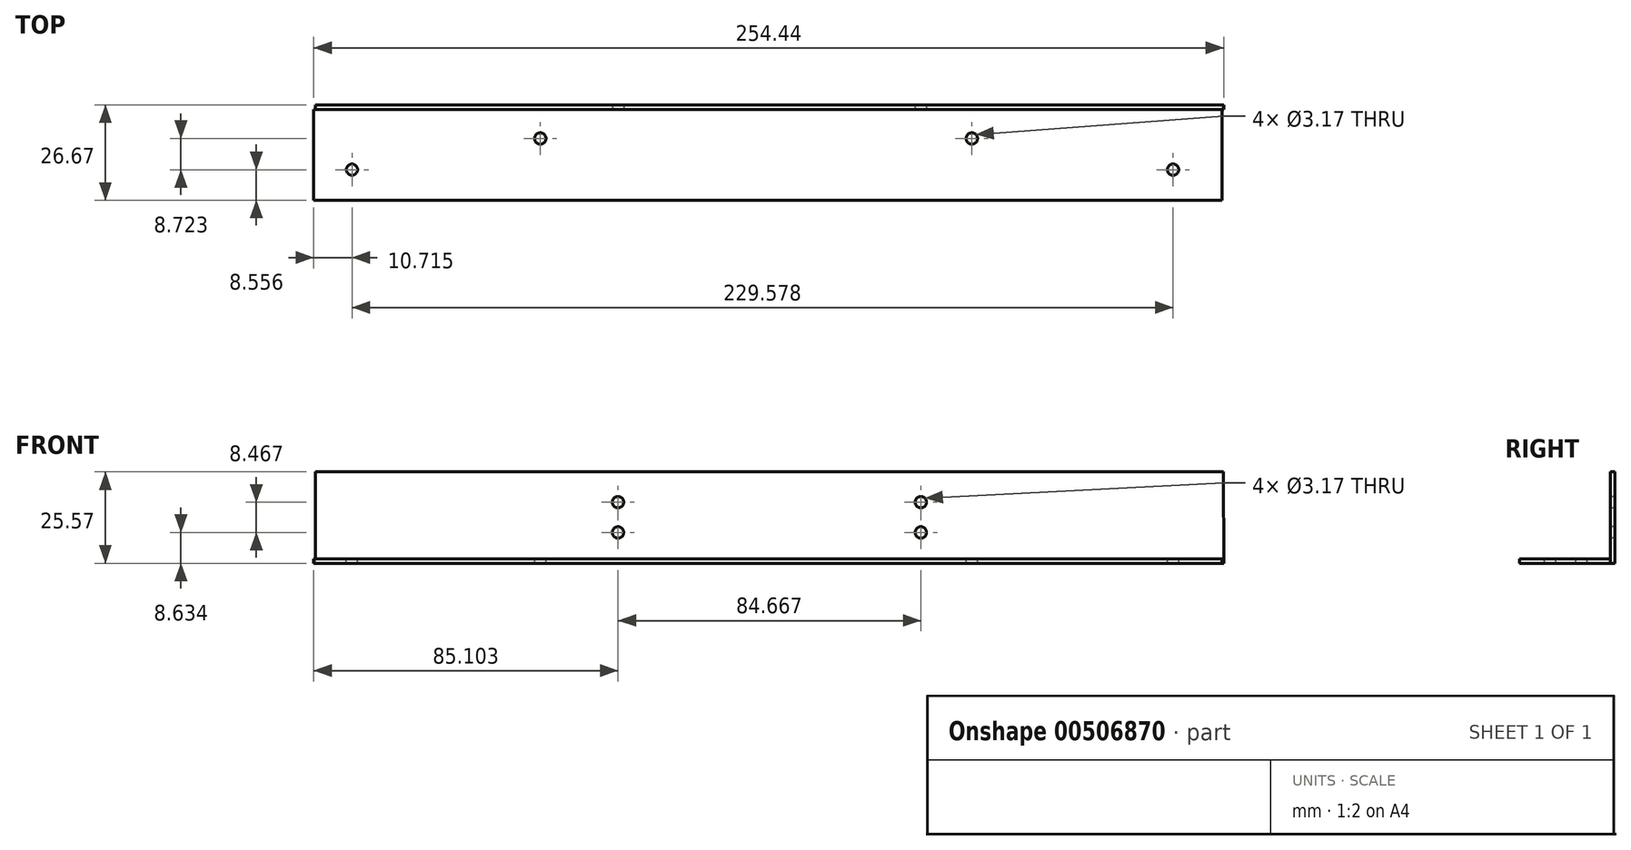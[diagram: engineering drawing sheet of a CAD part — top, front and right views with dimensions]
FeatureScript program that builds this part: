
annotation { "Feature Type Name" : "Feature", "Feature Type Description" : "" }
export const myFeature = defineFeature(function(context is Context, id is Id, definition is map)
    precondition{}
    {
        {
            var Q0;
            Q0=qCreatedBy(makeId("Front.planeOp"),FACE);
            var sketch = newSketch(context, id + "F0", { "sketchPlane" : qUnion([Q0])});
            skLineSegment(sketch, "E0", {"start": v(-131.8, 0) * mm, "end": v(122.2, 0) * mm});
            skLineSegment(sketch, "E1", {"start": v(-131.8, 0) * mm, "end": v(-131.8, 25.57) * mm});
            skLineSegment(sketch, "E2", {"start": v(-131.8, 25.57) * mm, "end": v(122.12, 25.57) * mm});
            skLineSegment(sketch, "E3", {"start": v(122.12, 25.57) * mm, "end": v(122.2, 0) * mm});
            skLineSegment(sketch, "E4", {"start": v(-47.14, 25.57) * mm, "end": v(-47.14, 0) * mm});
            skLineSegment(sketch, "E5", {"start": v(37.53, 25.57) * mm, "end": v(37.53, 0) * mm});
            skLineSegment(sketch, "E6", {"start": v(-47.14, 17.1) * mm, "end": v(37.53, 17.1) * mm});
            skLineSegment(sketch, "E7", {"start": v(-47.14, 8.63) * mm, "end": v(37.53, 8.63) * mm});
            skSolve(sketch);
        }
        {
            var Q0;
            Q0=qCreatedBy(makeId("Top.planeOp"),FACE);
            var sketch = newSketch(context, id + "F1", { "sketchPlane" : qUnion([Q0])});
            skLineSegment(sketch, "E8.bottom", {"start": v(-132.24, 0) * mm, "end": v(121.76, 0) * mm});
            skLineSegment(sketch, "E8.top", {"start": v(-132.24, -25.4) * mm, "end": v(121.76, -25.4) * mm});
            skLineSegment(sketch, "E8.left", {"start": v(-132.24, 0) * mm, "end": v(-132.24, -25.4) * mm});
            skLineSegment(sketch, "E8.right", {"start": v(121.76, 0) * mm, "end": v(121.76, -25.4) * mm});
            skLineSegment(sketch, "E9", {"start": v(-68.74, 0) * mm, "end": v(-68.74, -25.4) * mm, "construction": true});
            skLineSegment(sketch, "E10", {"start": v(-5.24, 0) * mm, "end": v(-5.24, -25.4) * mm, "construction": true});
            skLineSegment(sketch, "E11", {"start": v(58.26, 0) * mm, "end": v(58.26, -25.4) * mm, "construction": true});
            skLineSegment(sketch, "E12", {"start": v(-132.24, -8.47) * mm, "end": v(121.76, -8.47) * mm, "construction": true});
            skLineSegment(sketch, "E13", {"start": v(-132.24, -16.93) * mm, "end": v(121.76, -16.93) * mm, "construction": true});
            skSolve(sketch);
        }
        {
            var Q0;
            Q0=makeQuery(id+"F0.imprint","IMPRINT",FACE,{"disambiguationData":[TD([[makeQuery(id+"F0.imprint","IMPRINT",EDGE,{"derivedFrom":sQuery(id+"F0.wireOp",EDGE,"E0")}),1.0]])]});
            var Q1;
            {var subQ1=sQuery(id+"F0.wireOp",EDGE,"E1");Q1=makeQuery(id+"F0.imprint","IMPRINT",FACE,{"disambiguationData":[TD([[makeQuery(id+"F0.imprint","IMPRINT",EDGE,{"derivedFrom":subQ1}),-1.0]])]});}
            var Q2;
            {var subQ5=sQuery(id+"F0.wireOp",EDGE,"E6");Q2=makeQuery(id+"F0.imprint","IMPRINT",FACE,{"disambiguationData":[TD([[makeQuery(id+"F0.imprint","IMPRINT",EDGE,{"derivedFrom":subQ5}),1.0]])]});}
            var Q3;
            {var subQ0=sQuery(id+"F0.wireOp",EDGE,"E6");Q3=makeQuery(id+"F0.imprint","IMPRINT",FACE,{"disambiguationData":[TD([[makeQuery(id+"F0.imprint","IMPRINT",EDGE,{"derivedFrom":subQ0}),-1.0]])]});}
            var Q4;
            {var subQ4=sQuery(id+"F0.wireOp",EDGE,"E3");Q4=makeQuery(id+"F0.imprint","IMPRINT",FACE,{"disambiguationData":[TD([[makeQuery(id+"F0.imprint","IMPRINT",EDGE,{"derivedFrom":subQ4}),-1.0]])]});}
            extrude(context, id + "F2", {"entities" : qUnion([Q0, Q1, Q2, Q3, Q4]), "oppositeDirection" : true, "depth" : 1.27 * mm, "offsetDistance" : 25.4 * mm});
        }
        {
            var Q0;
            Q0=makeQuery(id+"F1.imprint","IMPRINT",FACE,{"disambiguationData":[TD([[makeQuery(id+"F1.imprint","IMPRINT",EDGE,{"derivedFrom":sQuery(id+"F1.wireOp",EDGE,"E8.bottom")}),-1.0]])]});
            extrude(context, id + "F3", {"entities" : qUnion([Q0]), "operationType" : NewBodyOperationType.ADD, "depth" : 1.27 * mm, "offsetDistance" : 25.4 * mm});
        }
        {
            var Q0;
            Q0=sQuery(id+"F0.wireOp",VERTEX,"E7.start");
            var Q1;
            Q1=sQuery(id+"F0.wireOp",VERTEX,"E7.end");
            var Q2;
            Q2=sQuery(id+"F0.wireOp",VERTEX,"E6.end");
            var Q3;
            Q3=sQuery(id+"F0.wireOp",VERTEX,"E6.start");
            var Q4;
            Q4=makeQuery(id+"F2.opExtrude","SWEPT_BODY",BODY,{"disambiguationData":[OSD([sQuery(id+"F0.wireOp",EDGE,"E0"),sQuery(id+"F0.wireOp",EDGE,"E1"),sQuery(id+"F0.wireOp",EDGE,"E2"),sQuery(id+"F0.wireOp",EDGE,"E3")])]});
            hole(context, id + "F4", {"style" : HoleStyle.SIMPLE, "endStyle" : HoleEndStyle.THROUGH, "holeDiameter" : 3.17 * mm, "isTappedThrough" : true, "tappedDepth" : 12.7 * mm, "tapClearance" : 3, "locations" : qUnion([Q0, Q1, Q2, Q3]), "scope" : qUnion([Q4])});
        }
        {
            var Q0;
            Q0=makeQuery(id+"F3.opExtrude","CAP_FACE",FACE,{"disambiguationData":[OSD([sQuery(id+"F1.wireOp",EDGE,"E8.bottom"),sQuery(id+"F1.wireOp",EDGE,"E8.top"),sQuery(id+"F1.wireOp",EDGE,"E8.left"),sQuery(id+"F1.wireOp",EDGE,"E8.right")])],"isStart":false});
            var sketch = newSketch(context, id + "F5", { "sketchPlane" : qUnion([Q0])});
            skPoint(sketch, "E14", {"position": v(-68.87, -8.12) * mm});
            skPoint(sketch, "E15.positionSnap0", {"position": v(-5.24, -25.4) * mm});
            skPoint(sketch, "E16", {"position": v(-121.52, -16.84) * mm});
            skPoint(sketch, "E17", {"position": v(51.79, -8.12) * mm});
            skPoint(sketch, "E18", {"position": v(108.05, -16.84) * mm});
            skSolve(sketch);
        }
        {
            var Q0;
            Q0=sQuery(id+"F5.wireOp",VERTEX,"E16");
            var Q1;
            Q1=sQuery(id+"F5.wireOp",VERTEX,"E14");
            var Q2;
            Q2=sQuery(id+"F5.wireOp",VERTEX,"E17");
            var Q3;
            Q3=sQuery(id+"F5.wireOp",VERTEX,"E18");
            var Q4;
            Q4=makeQuery(id+"F2.opExtrude","SWEPT_BODY",BODY,{"disambiguationData":[OSD([sQuery(id+"F0.wireOp",EDGE,"E0"),sQuery(id+"F0.wireOp",EDGE,"E1"),sQuery(id+"F0.wireOp",EDGE,"E2"),sQuery(id+"F0.wireOp",EDGE,"E3")])]});
            hole(context, id + "F6", {"style" : HoleStyle.SIMPLE, "endStyle" : HoleEndStyle.THROUGH, "holeDiameter" : 3.17 * mm, "isTappedThrough" : true, "tappedDepth" : 12.7 * mm, "tapClearance" : 3, "locations" : qUnion([Q0, Q1, Q2, Q3]), "scope" : qUnion([Q4])});
        }
    });
